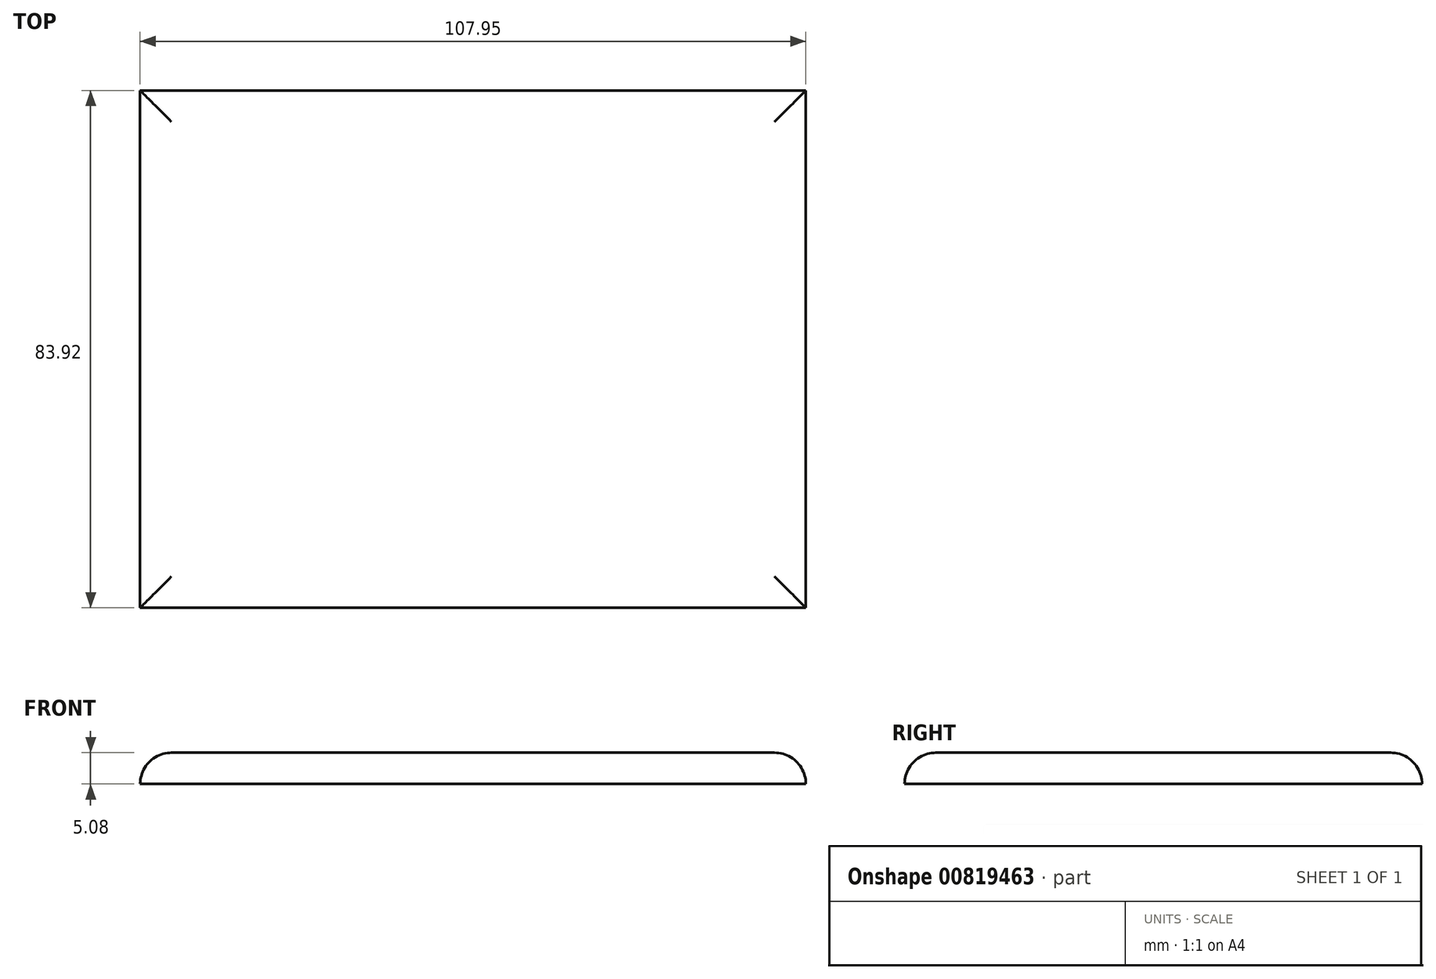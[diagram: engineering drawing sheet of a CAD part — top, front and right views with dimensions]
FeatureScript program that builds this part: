
annotation { "Feature Type Name" : "Feature", "Feature Type Description" : "" }
export const myFeature = defineFeature(function(context is Context, id is Id, definition is map)
    precondition{}
    {
        {
            var Q0;
            Q0=qCreatedBy(makeId("Top.planeOp"),FACE);
            var sketch = newSketch(context, id + "F0", { "sketchPlane" : qUnion([Q0])});
            skLineSegment(sketch, "E0.bottom", {"start": v(-52.13, 48.68) * mm, "end": v(55.82, 48.68) * mm});
            skLineSegment(sketch, "E0.top", {"start": v(-52.13, -35.24) * mm, "end": v(55.82, -35.24) * mm});
            skLineSegment(sketch, "E0.left", {"start": v(-52.13, 48.68) * mm, "end": v(-52.13, -35.24) * mm});
            skLineSegment(sketch, "E0.right", {"start": v(55.82, 48.68) * mm, "end": v(55.82, -35.24) * mm});
            skSolve(sketch);
        }
        {
            var Q0;
            Q0=makeQuery(id+"F0.imprint","IMPRINT",FACE,{"disambiguationData":[TD([[makeQuery(id+"F0.imprint","IMPRINT",EDGE,{"derivedFrom":sQuery(id+"F0.wireOp",EDGE,"E0.bottom")}),-1.0]])]});
            extrude(context, id + "F1", {"entities" : qUnion([Q0]), "depth" : 5.08 * mm, "offsetDistance" : 25.4 * mm});
        }
        {
            var Q0;
            Q0=makeQuery(id+"F1.opExtrude","CAP_EDGE",EDGE,{"disambiguationData":[OSD([sQuery(id+"F0.wireOp",EDGE,"E0.top")])],"isStart":false});
            var Q1;
            Q1=makeQuery(id+"F1.opExtrude","CAP_EDGE",EDGE,{"disambiguationData":[OSD([sQuery(id+"F0.wireOp",EDGE,"E0.right")])],"isStart":false});
            var Q2;
            Q2=makeQuery(id+"F1.opExtrude","CAP_EDGE",EDGE,{"disambiguationData":[OSD([sQuery(id+"F0.wireOp",EDGE,"E0.left")])],"isStart":false});
            var Q3;
            Q3=makeQuery(id+"F1.opExtrude","CAP_EDGE",EDGE,{"disambiguationData":[OSD([sQuery(id+"F0.wireOp",EDGE,"E0.bottom")])],"isStart":false});
            fillet(context, id + "F2", {"entities" : qUnion([Q0, Q1, Q2, Q3]), "radius" : 5.08 * mm, "tangentPropagation" : true, "allowEdgeOverflow" : false});
        }
    });
